# Revit family: CONV_Geberit_ShwrEnclsrs_IfoSpaceBifoldedSPNKB
name_source: partatom
category: Furniture
revit_build: Autodesk Revit 2016 (Build: 20150220_1215(x64)
units: mm (PartAtom-declared; Revit-internal decimal feet)

## family parameters
Always vertical = Yes
Cut with Voids When Loaded = No
OmniClass Number = 23.45.05.00
OmniClass Title = Sanitary Equipment
Room Calculation Point = No
Shared = No
Work Plane-Based = No

## types (6) — shared parameters
AssetType = Fixed
BIMObjectName = CONV_Geberit_ShwrEnclsrs_IfoSpaceBifoldedSPNKB
Brand = Ifo
Category = Shower enclosures
Collection = Ifo Space
Color = Transparent
DurationUnit = Year
ExpiringDate = 12/2018
Finish = Matt aluminium. Clear glass.
IfcExportAs = IfcFurnitureType
IfcExportType = NOTDEFINED
MainColor = Transparent
Manufacturer = Ifo (Geberit Group)
ManufacturerName = Ifo (Geberit Group)
ManufacturerURL = https://www.ifo.se
Material = Glass, metal
NBSDescription = Shower enclosures
NBSReference = 45-35-70/332
Name = ShwrEnclsrs_IfoSpaceBifoldedSPNKB
NominalDepth = 56 mm  [stored 0.183727 ft]
NominalHeight = 2000 mm  [stored 6.56168 ft]
ProductURL_DK = http://www.ifo.dk
ProductURL_NO = http://www.porsgrundbad.no
ProductURL_SE = http://www.ifo.se
Shape = Sculptured
ShowerEnclosureMainMaterial = Clear Glass
ShowerEnclosureSecondaryMaterial = Aluminium
URL = https://www.ifo.se
Uniclass2 = Pr_40_30_06_79
Uniclass2015Description = Shower enclosures
Uniclass2015Reference = Pr_40_20_06_79
Version = 1
VersionDate = 13/04/2018
WarrantyDurationUnit = Year
zero-valued in all types: Cost

## per-type parameters (varying)
| type | ConvergoRefNr | EANNumber | ModelNumber | NominalLength | Orientation | Size | Weight |
| Ifo Space Bifolded SPNKB - 700mm left | 0132-1802-0031-SE | 7391515444308 | 59702197 | 700 mm  [stored 2.29659 ft] | IDOShowerama1011-left | 685x34x2000mm | 24.1 kg |
| Ifo Space Bifolded SPNKB - 800mm left | 0132-1802-0033-SE | 7391515444414 | 59802197 | 800 mm  [stored 2.62467 ft] | IDOShowerama1011-left | 780x34x2000mm | 27 kg |
| Ifo Space Bifolded SPNKB - 900mm left | 0132-1802-0035-SE | 7391515444438 | 59902197 | 900 mm  [stored 2.95276 ft] | IDOShowerama1011-left | 885x34x2000mm | 29.9 kg |
| Ifo Space Bifolded SPNKB - 700mm right | 0132-1802-0032-SE | 7391515444407 | 59701197 | 700 mm  [stored 2.29659 ft] | IDOShowerama1011-right | 685x34x2000mm | 24.1 kg |
| Ifo Space Bifolded SPNKB - 800mm right | 0132-1802-0034-SE | 7391515444421 | 59801197 | 800 mm  [stored 2.62467 ft] | IDOShowerama1011-right | 780x34x2000mm | 27 kg |
| Ifo Space Bifolded SPNKB - 900mm right | 0132-1802-0036-SE | 7391515444445 | 59901197 | 900 mm  [stored 2.95276 ft] | IDOShowerama1011-right | 885x34x2000mm | 29.9 kg |

note: column(s) folded — value = type name in every type: Model

note: [stored X ft] marks values corroborated as IEEE doubles in the binary element streams (Revit-internal decimal feet)

## geometry (parser evidence)
native form markers: Sweep x9
no freeform markers — native parametric forms only
